# Revit family: Trim_Set-GROHE-Eurosmart-19458_Series
name_source: partatom
category: Plumbing Fixtures
revit_build: Autodesk Revit 2018 (Build: 20170223_1515(x64)
units: mm (PartAtom-declared; Revit-internal decimal feet)

## family parameters
Cut with Voids When Loaded = No
Host = Face
OmniClass Number = 23.45.05.14.17
OmniClass Title = Showers
Part Type = Normal
Room Calculation Point = No
Round Connector Dimension = Use Diameter
Shared = Yes

## types (2) — shared parameters
ADA Compliant = Yes
Assembly Code = D2010710
CW Connection = No
CWFU = 3
Default Elevation = 44"
Description = The Eurosmart Pressure Balance Valve Trim from GROHE has a contemporary design crafted to the exacting standards you expect from GROHE. Ergonomic metal handle is gently curved, combining comfort and reliability with every turn.
HW Connection = No
HWFU = 3
Height = 6 7/8"
IAPMO Compliance = • ADA • CSA B125.1 • ASME A112.18.1
Installation Type = Wall Mounted
Length = 3 9/16"
Manufacturer = Grohe
Price = Prices may vary. Please consult Manufacturer Representative for most up-to-date price list.
Product Documentation Link = https://americanstandard.box.com
Product Page URL = https://www.grohe.us
URL = https://www.grohe.us
Vent Connection = No
WFU = 4
Waste Connection = No
Width = 6 1/4"

## per-type parameters (varying)
| type | Finish | Material |
| 19458003 | Metal-Grohe-Starlight Chrome | Metal-Grohe-Starlight Chrome |
| 19458EN3 | Metal-Grohe-Brushed Nickel Infinity Finish | Metal-Grohe-Brushed Nickel Infinity Finish |

note: column(s) folded — value = type name in every type: Model

## geometry (parser evidence)
native form markers: Sweep x5
no freeform markers — native parametric forms only
